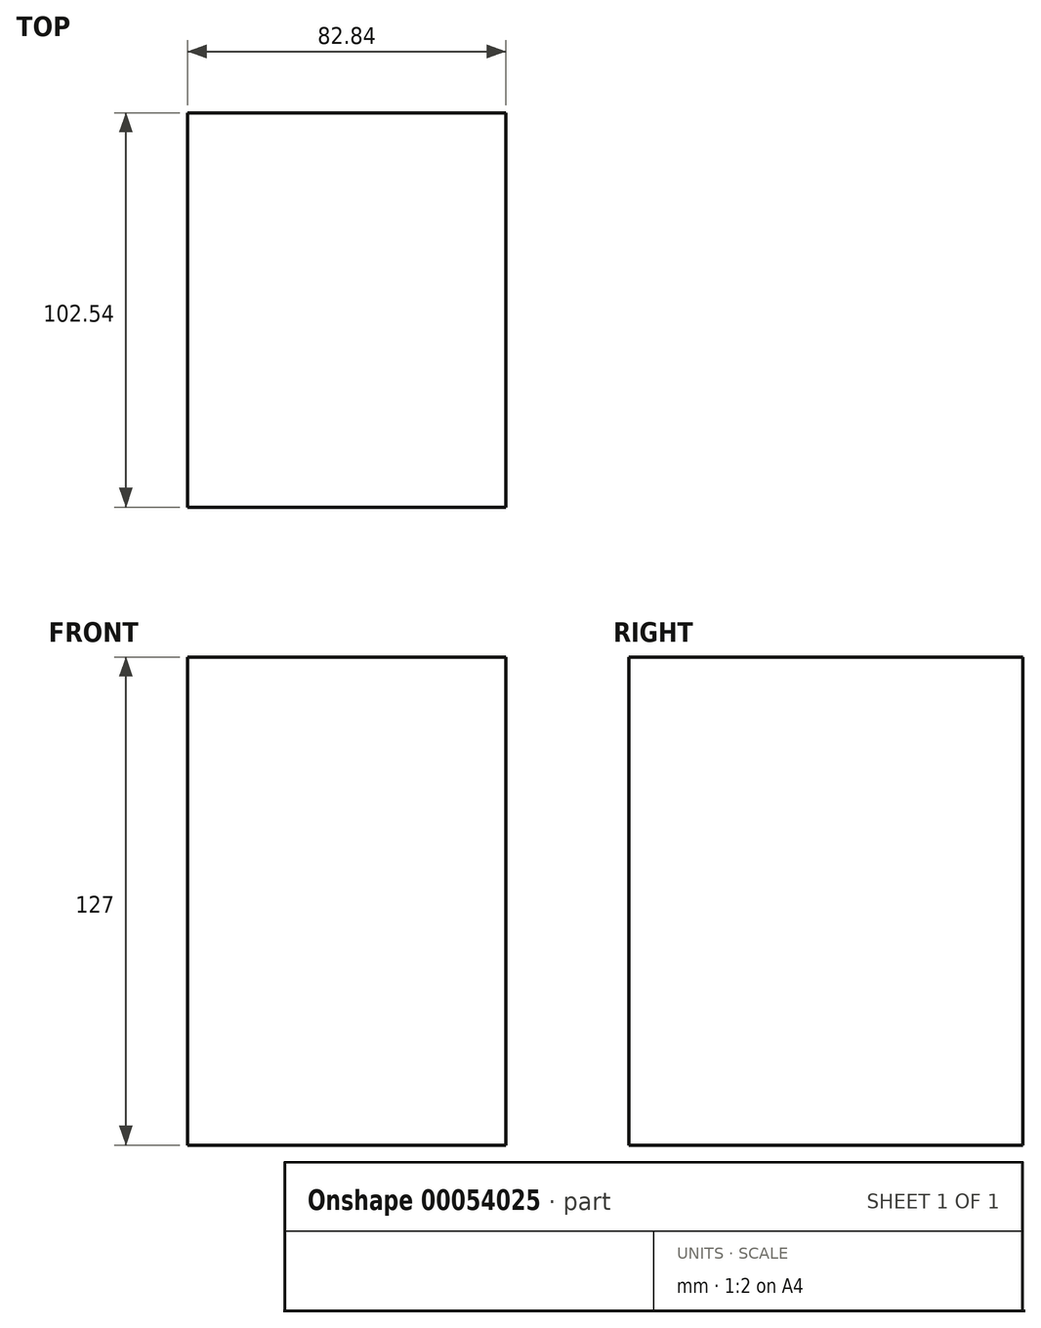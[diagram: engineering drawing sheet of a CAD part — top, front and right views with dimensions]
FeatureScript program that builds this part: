
annotation { "Feature Type Name" : "Feature", "Feature Type Description" : "" }
export const myFeature = defineFeature(function(context is Context, id is Id, definition is map)
    precondition{}
    {
        {
            var Q0;
            Q0=qCreatedBy(makeId("Top.planeOp"),FACE);
            var sketch = newSketch(context, id + "F0", { "sketchPlane" : qUnion([Q0])});
            skLineSegment(sketch, "E0.bottom", {"start": v(-38.32, 47.9) * mm, "end": v(44.52, 47.9) * mm});
            skLineSegment(sketch, "E0.top", {"start": v(-38.32, -54.64) * mm, "end": v(44.52, -54.64) * mm});
            skLineSegment(sketch, "E0.left", {"start": v(-38.32, 47.9) * mm, "end": v(-38.32, -54.64) * mm});
            skLineSegment(sketch, "E0.right", {"start": v(44.52, 47.9) * mm, "end": v(44.52, -54.64) * mm});
            skSolve(sketch);
        }
        {
            var Q0;
            Q0=makeQuery(id+"F0.imprint","IMPRINT",FACE,{"disambiguationData":[TD([[makeQuery(id+"F0.imprint","IMPRINT",EDGE,{"derivedFrom":sQuery(id+"F0.wireOp",EDGE,"E0.bottom")}),-1.0]])]});
            extrude(context, id + "F1", {"entities" : qUnion([Q0]), "depth" : 127 * mm});
        }
    });
